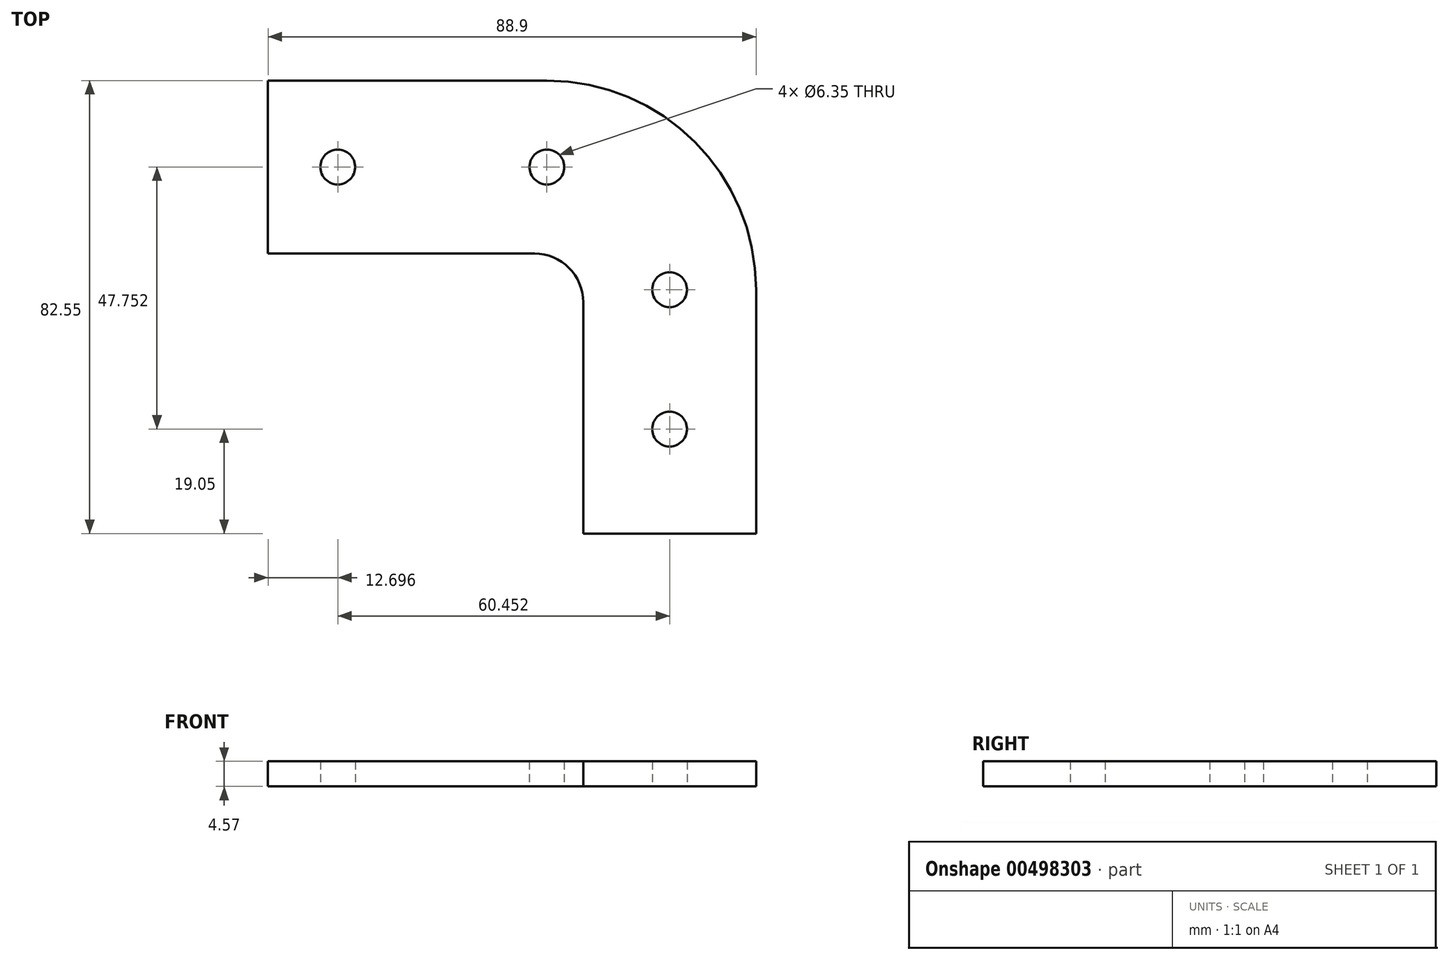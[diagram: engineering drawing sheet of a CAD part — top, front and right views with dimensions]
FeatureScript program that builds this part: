
annotation { "Feature Type Name" : "Feature", "Feature Type Description" : "" }
export const myFeature = defineFeature(function(context is Context, id is Id, definition is map)
    precondition{}
    {
        {
            var Q0;
            Q0=qCreatedBy(makeId("Top.planeOp"),FACE);
            var sketch = newSketch(context, id + "F0", { "sketchPlane" : qUnion([Q0])});
            skLineSegment(sketch, "E0", {"start": v(-57.4, 82.55) * mm, "end": v(-6.6, 82.55) * mm});
            skLineSegment(sketch, "E1", {"start": v(31.5, 44.45) * mm, "end": v(31.5, 0) * mm});
            skLineSegment(sketch, "E2", {"start": v(31.5, 0) * mm, "end": v(0, 0) * mm});
            skLineSegment(sketch, "E3", {"start": v(0, 0) * mm, "end": v(0, 42.16) * mm});
            skLineSegment(sketch, "E4", {"start": v(-8.9, 51.05) * mm, "end": v(-57.4, 51.05) * mm});
            skLineSegment(sketch, "E5", {"start": v(-57.4, 82.55) * mm, "end": v(-57.4, 51.05) * mm});
            skPoint(sketch, "E6.visualSharp", {"position": v(31.5, 82.55) * mm});
            skArc(sketch, "E6.filletArc", {"start": v(31.5, 44.45) * mm, "mid": v(20.34, 71.4) * mm, "end": v(-6.6, 82.55) * mm});
            skLineSegment(sketch, "E7", {"start": v(-57.4, 66.8) * mm, "end": v(-0.32, 66.8) * mm, "construction": true});
            skLineSegment(sketch, "E8", {"start": v(15.75, 0) * mm, "end": v(15.75, 50.73) * mm, "construction": true});
            skArc(sketch, "E9.filletArc", {"start": v(15.75, 50.73) * mm, "mid": v(11.04, 62.1) * mm, "end": v(-0.32, 66.8) * mm, "construction": true});
            skCircle(sketch, "E10", {"center": v(-44.7, 66.8) * mm, "radius": 3.18 * mm});
            skCircle(sketch, "E11", {"center": v(-6.6, 66.8) * mm, "radius": 3.18 * mm});
            skCircle(sketch, "E12", {"center": v(15.75, 44.45) * mm, "radius": 3.18 * mm});
            skCircle(sketch, "E13", {"center": v(15.75, 19.05) * mm, "radius": 3.18 * mm});
            skPoint(sketch, "E14.visualSharp", {"position": v(0, 51.05) * mm});
            skArc(sketch, "E14.filletArc", {"start": v(0, 42.16) * mm, "mid": v(-2.6, 48.45) * mm, "end": v(-8.9, 51.05) * mm});
            skSolve(sketch);
        }
        {
            var Q0;
            Q0=makeQuery(id+"F0.imprint","IMPRINT",FACE,{"disambiguationData":[TD([[makeQuery(id+"F0.imprint","IMPRINT",EDGE,{"derivedFrom":sQuery(id+"F0.wireOp",EDGE,"E0")}),-1.0]])]});
            extrude(context, id + "F1", {"entities" : qUnion([Q0]), "depth" : 4.57 * mm});
        }
    });
